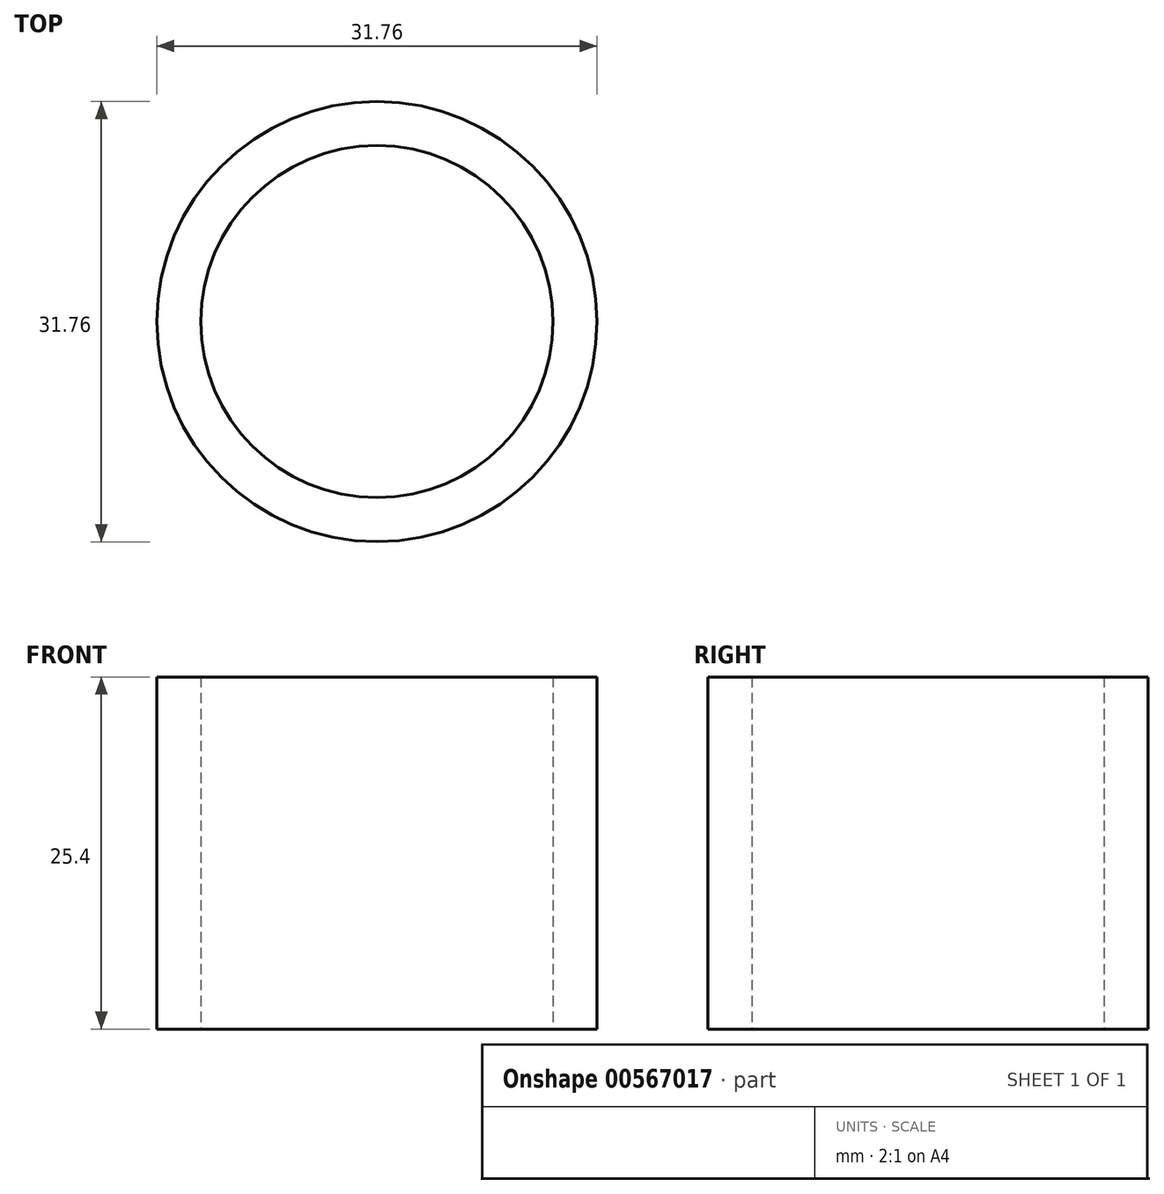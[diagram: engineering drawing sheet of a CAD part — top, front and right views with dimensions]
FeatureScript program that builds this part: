
annotation { "Feature Type Name" : "Feature", "Feature Type Description" : "" }
export const myFeature = defineFeature(function(context is Context, id is Id, definition is map)
    precondition{}
    {
        {
            var Q0;
            Q0=qCreatedBy(makeId("Top.planeOp"),FACE);
            var sketch = newSketch(context, id + "F0", { "sketchPlane" : qUnion([Q0])});
            skCircle(sketch, "E0", {"center": v(0, 0) * mm, "radius": 15.88 * mm});
            skCircle(sketch, "E1", {"center": v(0, 0) * mm, "radius": 12.7 * mm});
            skSolve(sketch);
        }
        {
            var Q0;
            Q0=makeQuery(id+"F0.imprint","IMPRINT",FACE,{"disambiguationData":[TD([[makeQuery(id+"F0.imprint","IMPRINT",EDGE,{"derivedFrom":sQuery(id+"F0.wireOp",EDGE,"E0")}),1.0]])]});
            extrude(context, id + "F1", {"entities" : qUnion([Q0]), "depth" : 25.4 * mm, "offsetDistance" : 25.4 * mm});
        }
    });
